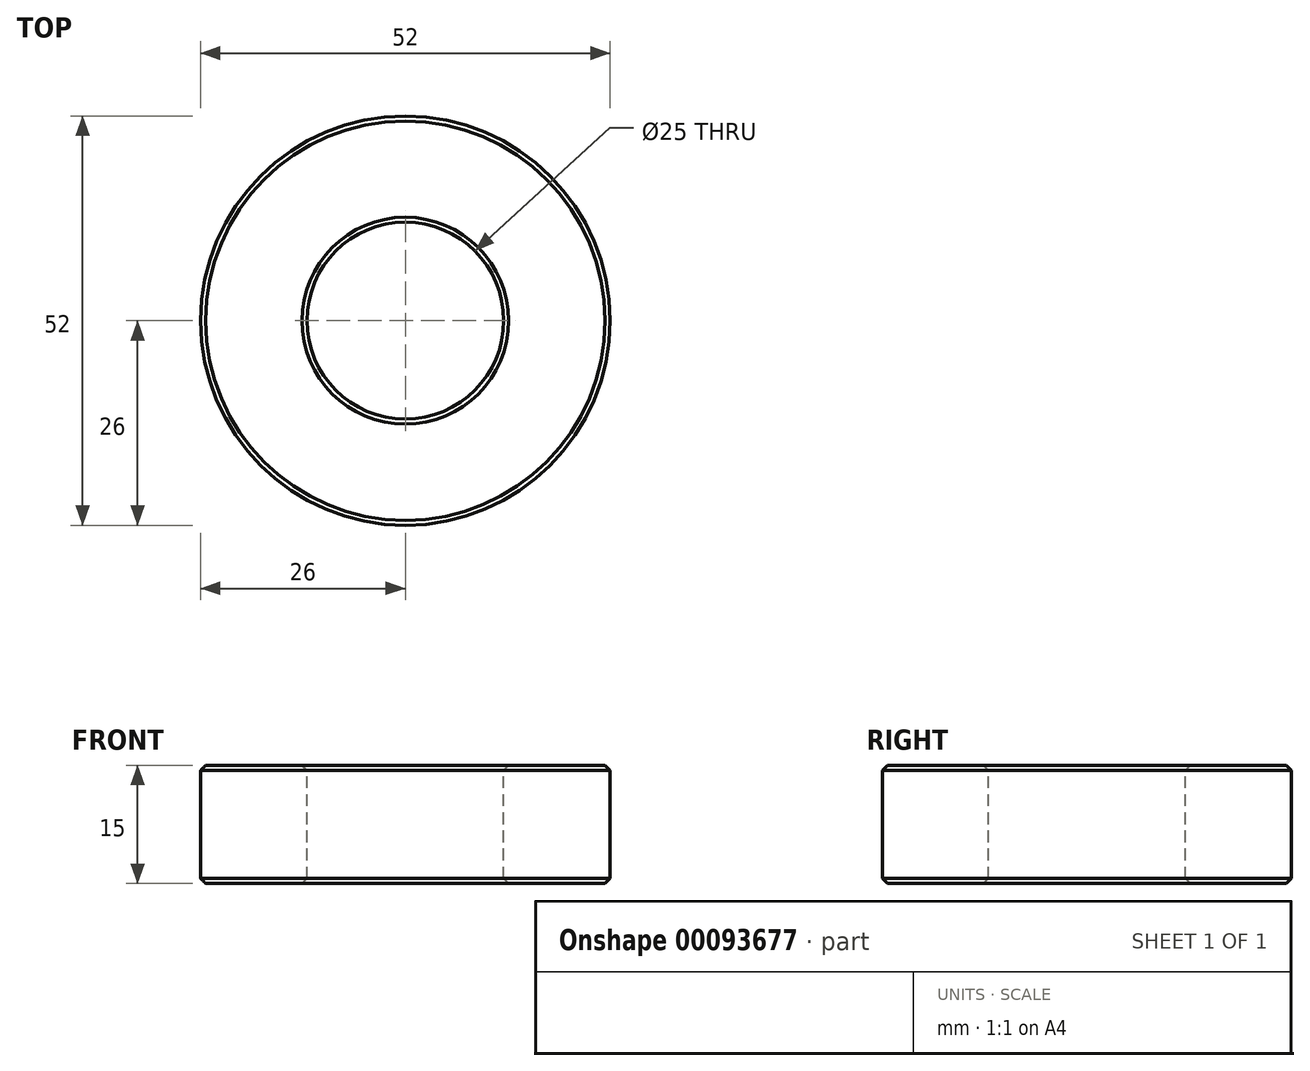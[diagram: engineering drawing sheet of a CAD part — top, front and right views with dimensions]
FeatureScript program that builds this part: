
annotation { "Feature Type Name" : "Feature", "Feature Type Description" : "" }
export const myFeature = defineFeature(function(context is Context, id is Id, definition is map)
    precondition{}
    {
        {
            var Q0;
            Q0=qCreatedBy(makeId("Front.planeOp"),FACE);
            var sketch = newSketch(context, id + "F0", { "sketchPlane" : qUnion([Q0])});
            skLineSegment(sketch, "E0", {"start": v(-26, 7.5) * mm, "end": v(-26, -7.5) * mm});
            skLineSegment(sketch, "E1", {"start": v(-26, -7.5) * mm, "end": v(-12.5, -7.5) * mm});
            skLineSegment(sketch, "E2", {"start": v(-12.5, -7.5) * mm, "end": v(-12.5, 7.5) * mm});
            skLineSegment(sketch, "E3", {"start": v(-26, 7.5) * mm, "end": v(-12.5, 7.5) * mm});
            skLineSegment(sketch, "E4", {"start": v(0, 26) * mm, "end": v(0, -19.2) * mm});
            skSolve(sketch);
        }
        {
            var Q0;
            Q0=qSketchRegion(id+"F0",true);
            var Q1;
            Q1=sQuery(id+"F0.wireOp",EDGE,"E4");
            revolve(context, id + "F1", {"entities" : qUnion([Q0]), "axis" : qUnion([Q1]), "revolveType" : RevolveType.FULL});
        }
        {
            var Q0;
            Q0=makeQuery(id+"F1.opRevolve","SWEPT_EDGE",EDGE,{"disambiguationData":[OSD([sQuery(id+"F0.wireOp",EDGE,"E0"),sQuery(id+"F0.wireOp",EDGE,"E3")])]});
            var Q1;
            Q1=makeQuery(id+"F1.opRevolve","SWEPT_EDGE",EDGE,{"disambiguationData":[OSD([sQuery(id+"F0.wireOp",EDGE,"E0"),sQuery(id+"F0.wireOp",EDGE,"E1")])]});
            var Q2;
            Q2=makeQuery(id+"F1.opRevolve","SWEPT_EDGE",EDGE,{"disambiguationData":[OSD([sQuery(id+"F0.wireOp",EDGE,"E2"),sQuery(id+"F0.wireOp",EDGE,"E3")])]});
            var Q3;
            Q3=makeQuery(id+"F1.opRevolve","SWEPT_EDGE",EDGE,{"disambiguationData":[OSD([sQuery(id+"F0.wireOp",EDGE,"E1"),sQuery(id+"F0.wireOp",EDGE,"E2")])]});
            chamfer(context, id + "F2", {"entities" : qUnion([Q0, Q1, Q2, Q3]), "width" : 0.64 * mm, "tangentPropagation" : true});
        }
    });
